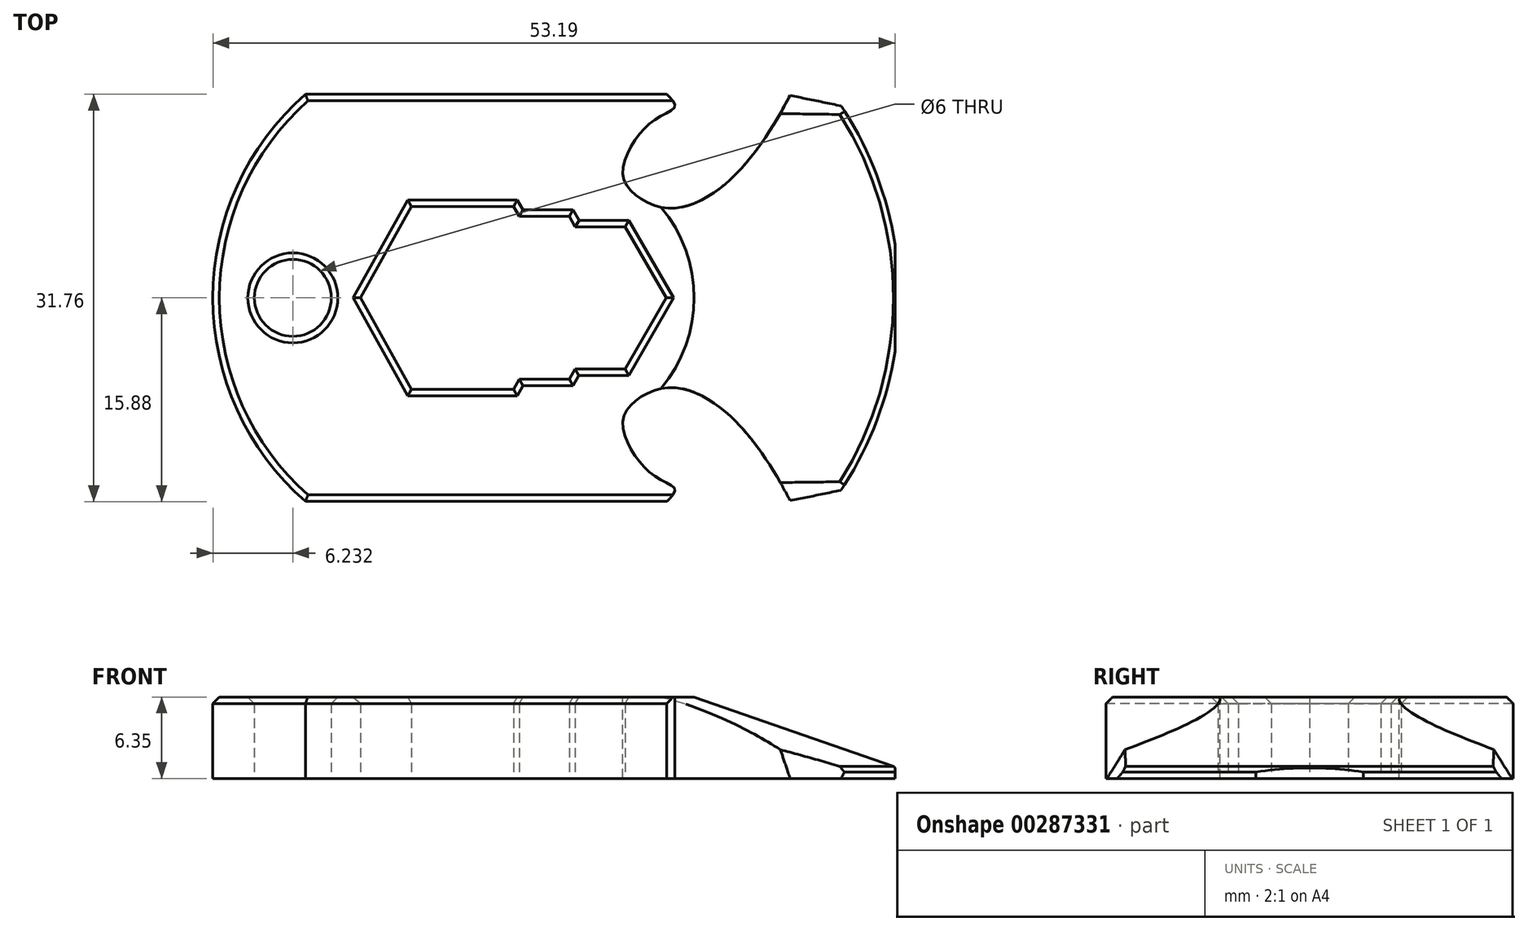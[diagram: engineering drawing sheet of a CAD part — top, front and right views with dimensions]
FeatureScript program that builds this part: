
annotation { "Feature Type Name" : "Feature", "Feature Type Description" : "" }
export const myFeature = defineFeature(function(context is Context, id is Id, definition is map)
    precondition{}
    {
        {
            var Q0;
            Q0=qCreatedBy(makeId("Top.planeOp"),FACE);
            var sketch = newSketch(context, id + "F0", { "sketchPlane" : qUnion([Q0])});
            skLineSegment(sketch, "E0.bottom", {"start": v(-25.4, 15.88) * mm, "end": v(25.4, 15.88) * mm});
            skLineSegment(sketch, "E0.top", {"start": v(-25.4, -15.87) * mm, "end": v(25.4, -15.87) * mm});
            skLineSegment(sketch, "E0.left", {"start": v(-25.4, 15.88) * mm, "end": v(-25.4, -15.87) * mm});
            skLineSegment(sketch, "E0.right", {"start": v(25.4, 15.87) * mm, "end": v(25.4, -15.87) * mm});
            skPoint(sketch, "E0.middle", {"position": v(0, 0) * mm});
            skLineSegment(sketch, "E1.MirrorCS", {"start": v(-76.2, 15.88) * mm, "end": v(-76.2, -15.87) * mm});
            skArc(sketch, "E2", {"start": v(-20.57, 15.87) * mm, "mid": v(-27.8, 0) * mm, "end": v(-20.57, -15.87) * mm});
            skArc(sketch, "E3", {"start": v(20.57, -15.87) * mm, "mid": v(25.72, 0) * mm, "end": v(20.57, 15.88) * mm});
            skCircle(sketch, "E4", {"center": v(-21.56, 0) * mm, "radius": 3 * mm});
            skLineSegment(sketch, "E5", {"start": v(-12.3, 7.14) * mm, "end": v(-16.27, 0) * mm});
            skLineSegment(sketch, "E6", {"start": v(-16.27, 0) * mm, "end": v(-12.3, -7.14) * mm});
            skLineSegment(sketch, "E7", {"start": v(-12.3, 7.14) * mm, "end": v(-4.35, 7.14) * mm});
            skLineSegment(sketch, "E8", {"start": v(-12.3, -7.14) * mm, "end": v(-4.35, -7.14) * mm});
            skLineSegment(sketch, "E9", {"start": v(-4.35, 7.14) * mm, "end": v(-3.9, 6.35) * mm});
            skLineSegment(sketch, "E10", {"start": v(-3.9, -6.35) * mm, "end": v(-4.35, -7.14) * mm});
            skLineSegment(sketch, "E11", {"start": v(-3.9, 6.35) * mm, "end": v(0, 6.35) * mm});
            skLineSegment(sketch, "E12", {"start": v(-3.9, -6.35) * mm, "end": v(0, -6.35) * mm});
            skLineSegment(sketch, "E13", {"start": v(0, 6.35) * mm, "end": v(0.46, 5.55) * mm});
            skLineSegment(sketch, "E14", {"start": v(0, -6.35) * mm, "end": v(0.46, -5.56) * mm});
            skLineSegment(sketch, "E15", {"start": v(0.46, 5.55) * mm, "end": v(4.35, 5.55) * mm});
            skLineSegment(sketch, "E16", {"start": v(0.46, -5.56) * mm, "end": v(4.34, -5.56) * mm});
            skLineSegment(sketch, "E17", {"start": v(4.35, 5.55) * mm, "end": v(7.56, 0) * mm});
            skLineSegment(sketch, "E18", {"start": v(4.34, -5.56) * mm, "end": v(7.56, 0) * mm});
            skArc(sketch, "E19", {"start": v(19.55, -15.88) * mm, "mid": v(24.54, 0) * mm, "end": v(19.55, 15.88) * mm});
            skFitSpline(sketch, "E20", {"points": [v(17.26, 15.87) * mm, v(15.73, 13.2) * mm, v(12.32, 9.02) * mm, v(8.3, 7) * mm, v(5.52, 7.77) * mm, v(4.2, 9.5) * mm, v(5.03, 12.15) * mm, v(6.97, 14.1) * mm, v(8.22, 14.93) * mm, v(7.6, 15.87) * mm], "startDerivative": vector(-11.4, -21.47) * mm, "endDerivative": vector(-14.56, 14.4) * mm});
            skFitSpline(sketch, "E21.MirrorCS", {"points": [v(17.26, -15.88) * mm, v(15.73, -13.2) * mm, v(12.32, -9.02) * mm, v(8.3, -7) * mm, v(5.52, -7.77) * mm, v(4.2, -9.5) * mm, v(5.03, -12.15) * mm, v(6.97, -14.1) * mm, v(8.22, -14.93) * mm, v(7.6, -15.88) * mm], "startDerivative": vector(-11.4, 21.47) * mm, "endDerivative": vector(-14.56, -14.4) * mm});
            skSolve(sketch);
        }
        {
            var Q0;
            {var subQ0=sQuery(id+"F0.wireOp",EDGE,"E2");var subQ1=sQuery(id+"F0.wireOp",EDGE,"E0.left");var subQ2=makeQuery(id+"F0.imprint","INTERSECT",VERTEX,{"disambiguationData":[OD(0.0)],"derivedFrom":[subQ1,subQ0]});Q0=makeQuery(id+"F0.imprint","IMPRINT",FACE,{"disambiguationData":[TD([[makeQuery(id+"F0.imprint","IMPRINT",EDGE,{"disambiguationData":[TD([[subQ2,-1.0]])],"derivedFrom":subQ1}),-1.0]])]});}
            var Q1;
            Q1=makeQuery(id+"F0.imprint","IMPRINT",FACE,{"disambiguationData":[TD([[makeQuery(id+"F0.imprint","IMPRINT",EDGE,{"derivedFrom":sQuery(id+"F0.wireOp",EDGE,"E4")}),-1.0]])]});
            var Q2;
            {var subQ0=sQuery(id+"F0.wireOp",EDGE,"E3");var subQ1=sQuery(id+"F0.wireOp",EDGE,"E0.right");var subQ2=makeQuery(id+"F0.imprint","INTERSECT",VERTEX,{"disambiguationData":[OD(0.0)],"derivedFrom":[subQ1,subQ0]});Q2=makeQuery(id+"F0.imprint","IMPRINT",FACE,{"disambiguationData":[TD([[makeQuery(id+"F0.imprint","IMPRINT",EDGE,{"disambiguationData":[TD([[subQ2,-1.0]])],"derivedFrom":subQ1}),1.0]])]});}
            var Q3;
            {var subQ5=sQuery(id+"F0.wireOp",EDGE,"E19");Q3=makeQuery(id+"F0.imprint","IMPRINT",FACE,{"disambiguationData":[TD([[makeQuery(id+"F0.imprint","IMPRINT",EDGE,{"derivedFrom":subQ5}),-1.0]])]});}
            extrude(context, id + "F1", {"entities" : qUnion([Q0, Q1, Q2, Q3]), "depth" : 6.35 * mm});
        }
        {
            var Q0;
            Q0=makeQuery(id+"F1.opExtrude","CAP_EDGE",EDGE,{"disambiguationData":[OSD([sQuery(id+"F0.wireOp",EDGE,"E3")])],"isStart":false});
            chamfer(context, id + "F2", {"entities" : qUnion([Q0]), "width" : 5.84 * mm, "tangentPropagation" : true});
        }
        {
            var Q0;
            Q0=makeQuery(id+"F1.opExtrude","CAP_EDGE",EDGE,{"disambiguationData":[OSD([sQuery(id+"F0.wireOp",EDGE,"E5")])],"isStart":false});
            chamfer(context, id + "F3", {"entities" : qUnion([Q0]), "width" : 0.5 * mm, "tangentPropagation" : true});
        }
        {
            var Q0;
            Q0=makeQuery(id+"F1.opExtrude","CAP_EDGE",EDGE,{"disambiguationData":[OSD([sQuery(id+"F0.wireOp",EDGE,"E6")])],"isStart":false});
            chamfer(context, id + "F4", {"entities" : qUnion([Q0]), "width" : 0.5 * mm, "tangentPropagation" : true});
        }
        {
            var Q0;
            Q0=makeQuery(id+"F1.opExtrude","CAP_EDGE",EDGE,{"disambiguationData":[OSD([sQuery(id+"F0.wireOp",EDGE,"E7")])],"isStart":false});
            var Q1;
            Q1=makeQuery(id+"F1.opExtrude","CAP_EDGE",EDGE,{"disambiguationData":[OSD([sQuery(id+"F0.wireOp",EDGE,"E8")])],"isStart":false});
            chamfer(context, id + "F5", {"entities" : qUnion([Q0, Q1]), "width" : 0.5 * mm, "tangentPropagation" : true});
        }
        {
            var Q0;
            Q0=makeQuery(id+"F1.opExtrude","CAP_EDGE",EDGE,{"disambiguationData":[OSD([sQuery(id+"F0.wireOp",EDGE,"E9")])],"isStart":false});
            chamfer(context, id + "F6", {"entities" : qUnion([Q0]), "width" : 0.5 * mm, "tangentPropagation" : true});
        }
        {
            var Q0;
            Q0=makeQuery(id+"F1.opExtrude","CAP_EDGE",EDGE,{"disambiguationData":[OSD([sQuery(id+"F0.wireOp",EDGE,"E11")])],"isStart":false});
            chamfer(context, id + "F7", {"entities" : qUnion([Q0]), "width" : 0.5 * mm, "tangentPropagation" : true});
        }
        {
            var Q0;
            Q0=makeQuery(id+"F1.opExtrude","CAP_EDGE",EDGE,{"disambiguationData":[OSD([sQuery(id+"F0.wireOp",EDGE,"E13")])],"isStart":false});
            chamfer(context, id + "F8", {"entities" : qUnion([Q0]), "width" : 0.5 * mm, "tangentPropagation" : true});
        }
        {
            var Q0;
            Q0=makeQuery(id+"F1.opExtrude","CAP_EDGE",EDGE,{"disambiguationData":[OSD([sQuery(id+"F0.wireOp",EDGE,"E15")])],"isStart":false});
            chamfer(context, id + "F9", {"entities" : qUnion([Q0]), "width" : 0.5 * mm, "tangentPropagation" : true});
        }
        {
            var Q0;
            Q0=makeQuery(id+"F1.opExtrude","CAP_EDGE",EDGE,{"disambiguationData":[OSD([sQuery(id+"F0.wireOp",EDGE,"E17")])],"isStart":false});
            chamfer(context, id + "F10", {"entities" : qUnion([Q0]), "width" : 0.5 * mm, "tangentPropagation" : true});
        }
        {
            var Q0;
            Q0=makeQuery(id+"F1.opExtrude","CAP_EDGE",EDGE,{"disambiguationData":[OSD([sQuery(id+"F0.wireOp",EDGE,"E10")])],"isStart":false});
            var Q1;
            Q1=makeQuery(id+"F1.opExtrude","CAP_EDGE",EDGE,{"disambiguationData":[OSD([sQuery(id+"F0.wireOp",EDGE,"E12")])],"isStart":false});
            var Q2;
            Q2=makeQuery(id+"F1.opExtrude","CAP_EDGE",EDGE,{"disambiguationData":[OSD([sQuery(id+"F0.wireOp",EDGE,"E14")])],"isStart":false});
            var Q3;
            Q3=makeQuery(id+"F1.opExtrude","CAP_EDGE",EDGE,{"disambiguationData":[OSD([sQuery(id+"F0.wireOp",EDGE,"E16")])],"isStart":false});
            var Q4;
            Q4=makeQuery(id+"F1.opExtrude","CAP_EDGE",EDGE,{"disambiguationData":[OSD([sQuery(id+"F0.wireOp",EDGE,"E18")])],"isStart":false});
            chamfer(context, id + "F11", {"entities" : qUnion([Q0, Q1, Q2, Q3, Q4]), "width" : 0.5 * mm, "tangentPropagation" : true});
        }
        {
            var Q0;
            {var subQ0=sQuery(id+"F0.wireOp",EDGE,"E0.top");Q0=makeQuery(id+"F1.opExtrude","CAP_EDGE",EDGE,{"disambiguationData":[OSD([subQ0]),TDD([makeQuery(id+"F0.imprint","IMPRINT",EDGE,{"disambiguationData":[TD([[makeQuery(id+"F0.imprint","INTERSECT",VERTEX,{"derivedFrom":[subQ0,sQuery(id+"F0.wireOp",EDGE,"E2")]}),-1.0]])],"derivedFrom":subQ0})])],"isStart":false});}
            var Q1;
            {var subQ0=sQuery(id+"F0.wireOp",EDGE,"E0.bottom");Q1=makeQuery(id+"F1.opExtrude","CAP_EDGE",EDGE,{"disambiguationData":[OSD([subQ0]),TDD([makeQuery(id+"F0.imprint","IMPRINT",EDGE,{"disambiguationData":[TD([[makeQuery(id+"F0.imprint","INTERSECT",VERTEX,{"derivedFrom":[subQ0,sQuery(id+"F0.wireOp",EDGE,"E2")]}),-1.0]])],"derivedFrom":subQ0})])],"isStart":false});}
            chamfer(context, id + "F12", {"entities" : qUnion([Q0, Q1]), "width" : 0.5 * mm, "tangentPropagation" : true});
        }
        {
            var Q0;
            Q0=makeQuery(id+"F1.opExtrude","CAP_EDGE",EDGE,{"disambiguationData":[OSD([sQuery(id+"F0.wireOp",EDGE,"E2")])],"isStart":false});
            chamfer(context, id + "F13", {"entities" : qUnion([Q0]), "width" : 0.5 * mm, "tangentPropagation" : true});
        }
        {
            var Q0;
            {var subQ0=sQuery(id+"F0.wireOp",EDGE,"E3");Q0=makeQuery(id+"F2.opChamfer","BLEND_EDGE",EDGE,{"blendedFrom":[makeQuery(id+"F1.opExtrude","CAP_EDGE",EDGE,{"disambiguationData":[OSD([subQ0])],"isStart":false}),makeQuery(id+"F1.opExtrude","CAP_FACE",FACE,{"disambiguationData":[OSD([sQuery(id+"F0.wireOp",EDGE,"E0.bottom"),sQuery(id+"F0.wireOp",EDGE,"E0.top"),sQuery(id+"F0.wireOp",EDGE,"E2"),subQ0,sQuery(id+"F0.wireOp",EDGE,"E4"),sQuery(id+"F0.wireOp",EDGE,"E5"),sQuery(id+"F0.wireOp",EDGE,"E6"),sQuery(id+"F0.wireOp",EDGE,"E7"),sQuery(id+"F0.wireOp",EDGE,"E8"),sQuery(id+"F0.wireOp",EDGE,"E9"),sQuery(id+"F0.wireOp",EDGE,"E10"),sQuery(id+"F0.wireOp",EDGE,"E11"),sQuery(id+"F0.wireOp",EDGE,"E12"),sQuery(id+"F0.wireOp",EDGE,"E13"),sQuery(id+"F0.wireOp",EDGE,"E14"),sQuery(id+"F0.wireOp",EDGE,"E15"),sQuery(id+"F0.wireOp",EDGE,"E16"),sQuery(id+"F0.wireOp",EDGE,"E17"),sQuery(id+"F0.wireOp",EDGE,"E18"),sQuery(id+"F0.wireOp",EDGE,"E20"),sQuery(id+"F0.wireOp",EDGE,"E21.MirrorCS")])],"isStart":false})],"blendedInto":[makeQuery(id+"F1.opExtrude","CAP_FACE",FACE,{"disambiguationData":[OSD([sQuery(id+"F0.wireOp",EDGE,"E0.bottom"),sQuery(id+"F0.wireOp",EDGE,"E0.top"),sQuery(id+"F0.wireOp",EDGE,"E2"),subQ0,sQuery(id+"F0.wireOp",EDGE,"E4"),sQuery(id+"F0.wireOp",EDGE,"E5"),sQuery(id+"F0.wireOp",EDGE,"E6"),sQuery(id+"F0.wireOp",EDGE,"E7"),sQuery(id+"F0.wireOp",EDGE,"E8"),sQuery(id+"F0.wireOp",EDGE,"E9"),sQuery(id+"F0.wireOp",EDGE,"E10"),sQuery(id+"F0.wireOp",EDGE,"E11"),sQuery(id+"F0.wireOp",EDGE,"E12"),sQuery(id+"F0.wireOp",EDGE,"E13"),sQuery(id+"F0.wireOp",EDGE,"E14"),sQuery(id+"F0.wireOp",EDGE,"E15"),sQuery(id+"F0.wireOp",EDGE,"E16"),sQuery(id+"F0.wireOp",EDGE,"E17"),sQuery(id+"F0.wireOp",EDGE,"E18"),sQuery(id+"F0.wireOp",EDGE,"E20"),sQuery(id+"F0.wireOp",EDGE,"E21.MirrorCS")])],"isStart":false})]});}
            chamfer(context, id + "F14", {"entities" : qUnion([Q0]), "chamferType" : ChamferType.TWO_OFFSETS, "width1" : 10.16 * mm, "oppositeDirection" : false, "width2" : 7.62 * mm, "tangentPropagation" : true});
        }
        {
            var Q0;
            {var subQ0=sQuery(id+"F0.wireOp",EDGE,"E3");var subQ1=sQuery(id+"F0.wireOp",EDGE,"E0.top");var subQ2=makeQuery(id+"F0.imprint","INTERSECT",VERTEX,{"derivedFrom":[subQ1,sQuery(id+"F0.wireOp",EDGE,"E19")]});var subQ3=sQuery(id+"F0.wireOp",EDGE,"E21.MirrorCS");Q0=makeQuery(id+"F14.opChamfer","BLEND_EDGE",EDGE,{"blendedFrom":[makeQuery(id+"F2.opChamfer","BLEND_EDGE",EDGE,{"blendedFrom":[makeQuery(id+"F1.opExtrude","CAP_EDGE",EDGE,{"disambiguationData":[OSD([subQ0])],"isStart":false}),makeQuery(id+"F1.opExtrude","CAP_FACE",FACE,{"disambiguationData":[OSD([sQuery(id+"F0.wireOp",EDGE,"E0.bottom"),subQ1,sQuery(id+"F0.wireOp",EDGE,"E2"),subQ0,sQuery(id+"F0.wireOp",EDGE,"E4"),sQuery(id+"F0.wireOp",EDGE,"E5"),sQuery(id+"F0.wireOp",EDGE,"E6"),sQuery(id+"F0.wireOp",EDGE,"E7"),sQuery(id+"F0.wireOp",EDGE,"E8"),sQuery(id+"F0.wireOp",EDGE,"E9"),sQuery(id+"F0.wireOp",EDGE,"E10"),sQuery(id+"F0.wireOp",EDGE,"E11"),sQuery(id+"F0.wireOp",EDGE,"E12"),sQuery(id+"F0.wireOp",EDGE,"E13"),sQuery(id+"F0.wireOp",EDGE,"E14"),sQuery(id+"F0.wireOp",EDGE,"E15"),sQuery(id+"F0.wireOp",EDGE,"E16"),sQuery(id+"F0.wireOp",EDGE,"E17"),sQuery(id+"F0.wireOp",EDGE,"E18"),sQuery(id+"F0.wireOp",EDGE,"E20"),subQ3])],"isStart":false})],"blendedInto":[makeQuery(id+"F1.opExtrude","CAP_FACE",FACE,{"disambiguationData":[OSD([sQuery(id+"F0.wireOp",EDGE,"E0.bottom"),subQ1,sQuery(id+"F0.wireOp",EDGE,"E2"),subQ0,sQuery(id+"F0.wireOp",EDGE,"E4"),sQuery(id+"F0.wireOp",EDGE,"E5"),sQuery(id+"F0.wireOp",EDGE,"E6"),sQuery(id+"F0.wireOp",EDGE,"E7"),sQuery(id+"F0.wireOp",EDGE,"E8"),sQuery(id+"F0.wireOp",EDGE,"E9"),sQuery(id+"F0.wireOp",EDGE,"E10"),sQuery(id+"F0.wireOp",EDGE,"E11"),sQuery(id+"F0.wireOp",EDGE,"E12"),sQuery(id+"F0.wireOp",EDGE,"E13"),sQuery(id+"F0.wireOp",EDGE,"E14"),sQuery(id+"F0.wireOp",EDGE,"E15"),sQuery(id+"F0.wireOp",EDGE,"E16"),sQuery(id+"F0.wireOp",EDGE,"E17"),sQuery(id+"F0.wireOp",EDGE,"E18"),sQuery(id+"F0.wireOp",EDGE,"E20"),subQ3])],"isStart":false})]}),makeQuery(id+"F1.opExtrude","SWEPT_FACE",FACE,{"disambiguationData":[OSD([subQ1]),TDD([makeQuery(id+"F0.imprint","IMPRINT",EDGE,{"disambiguationData":[TD([[subQ2,1.0]])],"derivedFrom":subQ1}),makeQuery(id+"F0.imprint","IMPRINT",EDGE,{"disambiguationData":[TD([[makeQuery(id+"F0.imprint","INTERSECT",VERTEX,{"derivedFrom":[subQ1,subQ0]}),1.0]])],"derivedFrom":subQ1})])]})],"blendedInto":[makeQuery(id+"F1.opExtrude","SWEPT_FACE",FACE,{"disambiguationData":[OSD([subQ1]),TDD([makeQuery(id+"F0.imprint","IMPRINT",EDGE,{"disambiguationData":[TD([[subQ2,1.0]])],"derivedFrom":subQ1}),makeQuery(id+"F0.imprint","IMPRINT",EDGE,{"disambiguationData":[TD([[makeQuery(id+"F0.imprint","INTERSECT",VERTEX,{"derivedFrom":[subQ1,subQ0]}),1.0]])],"derivedFrom":subQ1})])]})]});}
            chamfer(context, id + "F15", {"entities" : qUnion([Q0]), "chamferType" : ChamferType.TWO_OFFSETS, "width1" : 1.78 * mm, "oppositeDirection" : false, "width2" : 1.52 * mm, "tangentPropagation" : true});
        }
        {
            var Q0;
            {var subQ0=sQuery(id+"F0.wireOp",EDGE,"E3");var subQ1=sQuery(id+"F0.wireOp",EDGE,"E0.bottom");var subQ2=makeQuery(id+"F0.imprint","INTERSECT",VERTEX,{"derivedFrom":[subQ1,sQuery(id+"F0.wireOp",EDGE,"E19")]});var subQ3=sQuery(id+"F0.wireOp",EDGE,"E20");Q0=makeQuery(id+"F14.opChamfer","BLEND_EDGE",EDGE,{"blendedFrom":[makeQuery(id+"F2.opChamfer","BLEND_EDGE",EDGE,{"blendedFrom":[makeQuery(id+"F1.opExtrude","CAP_EDGE",EDGE,{"disambiguationData":[OSD([subQ0])],"isStart":false}),makeQuery(id+"F1.opExtrude","CAP_FACE",FACE,{"disambiguationData":[OSD([subQ1,sQuery(id+"F0.wireOp",EDGE,"E0.top"),sQuery(id+"F0.wireOp",EDGE,"E2"),subQ0,sQuery(id+"F0.wireOp",EDGE,"E4"),sQuery(id+"F0.wireOp",EDGE,"E5"),sQuery(id+"F0.wireOp",EDGE,"E6"),sQuery(id+"F0.wireOp",EDGE,"E7"),sQuery(id+"F0.wireOp",EDGE,"E8"),sQuery(id+"F0.wireOp",EDGE,"E9"),sQuery(id+"F0.wireOp",EDGE,"E10"),sQuery(id+"F0.wireOp",EDGE,"E11"),sQuery(id+"F0.wireOp",EDGE,"E12"),sQuery(id+"F0.wireOp",EDGE,"E13"),sQuery(id+"F0.wireOp",EDGE,"E14"),sQuery(id+"F0.wireOp",EDGE,"E15"),sQuery(id+"F0.wireOp",EDGE,"E16"),sQuery(id+"F0.wireOp",EDGE,"E17"),sQuery(id+"F0.wireOp",EDGE,"E18"),subQ3,sQuery(id+"F0.wireOp",EDGE,"E21.MirrorCS")])],"isStart":false})],"blendedInto":[makeQuery(id+"F1.opExtrude","CAP_FACE",FACE,{"disambiguationData":[OSD([subQ1,sQuery(id+"F0.wireOp",EDGE,"E0.top"),sQuery(id+"F0.wireOp",EDGE,"E2"),subQ0,sQuery(id+"F0.wireOp",EDGE,"E4"),sQuery(id+"F0.wireOp",EDGE,"E5"),sQuery(id+"F0.wireOp",EDGE,"E6"),sQuery(id+"F0.wireOp",EDGE,"E7"),sQuery(id+"F0.wireOp",EDGE,"E8"),sQuery(id+"F0.wireOp",EDGE,"E9"),sQuery(id+"F0.wireOp",EDGE,"E10"),sQuery(id+"F0.wireOp",EDGE,"E11"),sQuery(id+"F0.wireOp",EDGE,"E12"),sQuery(id+"F0.wireOp",EDGE,"E13"),sQuery(id+"F0.wireOp",EDGE,"E14"),sQuery(id+"F0.wireOp",EDGE,"E15"),sQuery(id+"F0.wireOp",EDGE,"E16"),sQuery(id+"F0.wireOp",EDGE,"E17"),sQuery(id+"F0.wireOp",EDGE,"E18"),subQ3,sQuery(id+"F0.wireOp",EDGE,"E21.MirrorCS")])],"isStart":false})]}),makeQuery(id+"F1.opExtrude","SWEPT_FACE",FACE,{"disambiguationData":[OSD([subQ1]),TDD([makeQuery(id+"F0.imprint","IMPRINT",EDGE,{"disambiguationData":[TD([[subQ2,1.0]])],"derivedFrom":subQ1}),makeQuery(id+"F0.imprint","IMPRINT",EDGE,{"disambiguationData":[TD([[makeQuery(id+"F0.imprint","INTERSECT",VERTEX,{"derivedFrom":[subQ1,subQ0]}),1.0]])],"derivedFrom":subQ1})])]})],"blendedInto":[makeQuery(id+"F1.opExtrude","SWEPT_FACE",FACE,{"disambiguationData":[OSD([subQ1]),TDD([makeQuery(id+"F0.imprint","IMPRINT",EDGE,{"disambiguationData":[TD([[subQ2,1.0]])],"derivedFrom":subQ1}),makeQuery(id+"F0.imprint","IMPRINT",EDGE,{"disambiguationData":[TD([[makeQuery(id+"F0.imprint","INTERSECT",VERTEX,{"derivedFrom":[subQ1,subQ0]}),1.0]])],"derivedFrom":subQ1})])]})]});}
            chamfer(context, id + "F16", {"entities" : qUnion([Q0]), "chamferType" : ChamferType.TWO_OFFSETS, "width1" : 1.78 * mm, "oppositeDirection" : false, "width2" : 1.52 * mm, "tangentPropagation" : true});
        }
        {
            var Q0;
            Q0=makeQuery(id+"F1.opExtrude","CAP_EDGE",EDGE,{"disambiguationData":[OSD([sQuery(id+"F0.wireOp",EDGE,"E4")])],"isStart":false});
            chamfer(context, id + "F17", {"entities" : qUnion([Q0]), "width" : 0.5 * mm, "tangentPropagation" : true});
        }
    });
